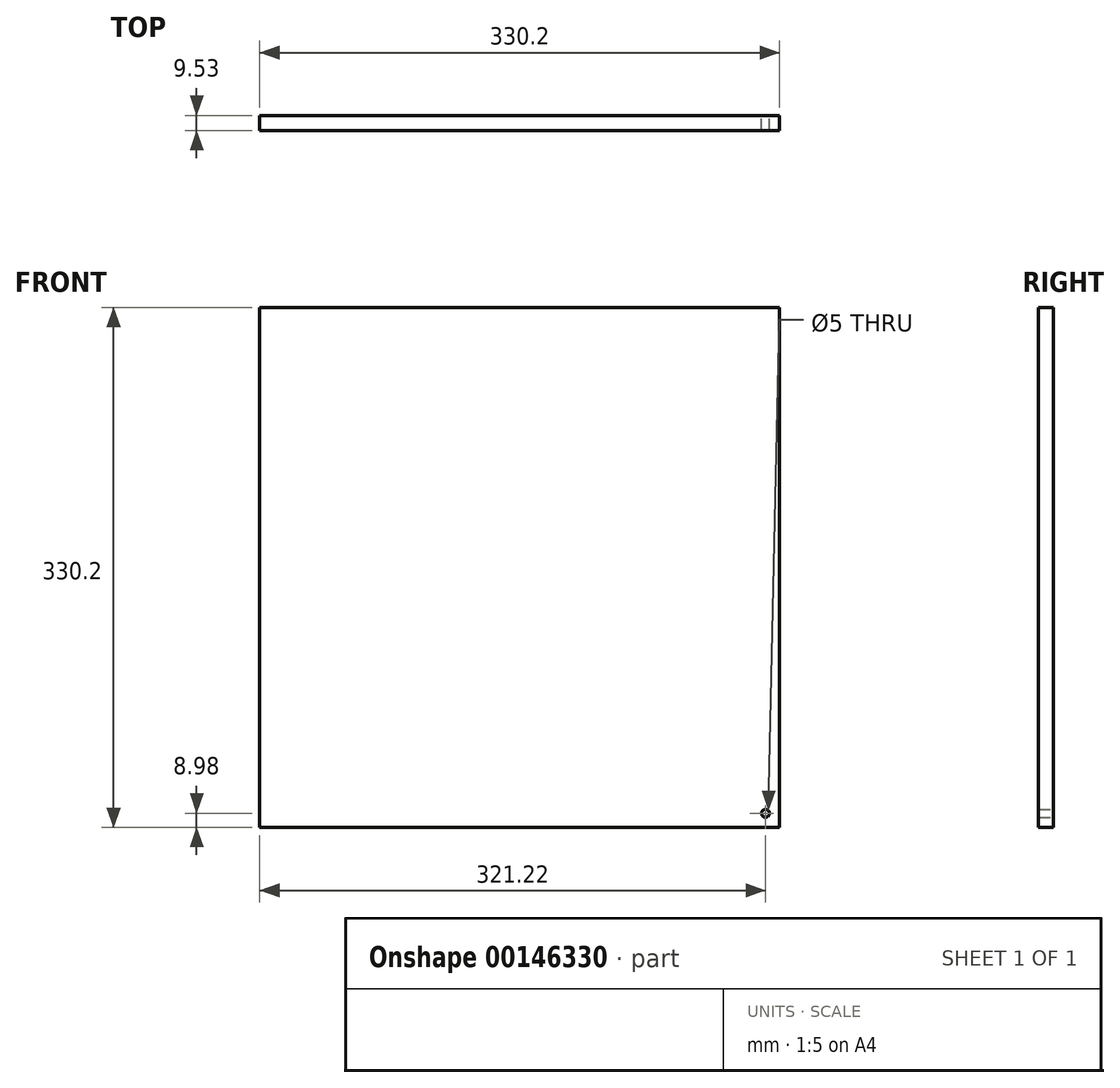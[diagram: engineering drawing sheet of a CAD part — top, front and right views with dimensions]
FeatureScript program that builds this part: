
annotation { "Feature Type Name" : "Feature", "Feature Type Description" : "" }
export const myFeature = defineFeature(function(context is Context, id is Id, definition is map)
    precondition{}
    {
        {
            var Q0;
            Q0=qCreatedBy(makeId("Front.planeOp"),FACE);
            var sketch = newSketch(context, id + "F0", { "sketchPlane" : qUnion([Q0])});
            skLineSegment(sketch, "E0.bottom", {"start": v(0, 0) * mm, "end": v(330.2, 0) * mm});
            skLineSegment(sketch, "E0.top", {"start": v(0, 330.2) * mm, "end": v(330.2, 330.2) * mm});
            skLineSegment(sketch, "E0.left", {"start": v(0, 0) * mm, "end": v(0, 330.2) * mm});
            skLineSegment(sketch, "E0.right", {"start": v(330.2, 0) * mm, "end": v(330.2, 330.2) * mm});
            skSolve(sketch);
        }
        {
            var Q0;
            Q0 = qSketchRegion(id + "F0", true);
            var Q1;
            Q1=makeQuery(id+"F0.imprint","IMPRINT",FACE,{"disambiguationData":[TD([[makeQuery(id+"F0.imprint","IMPRINT",EDGE,{"derivedFrom":sQuery(id+"F0.wireOp",EDGE,"E0.bottom")}),1.0]])]});
            extrude(context, id + "F1", {"entities" : qUnion([Q0, Q1]), "depth" : 9.52 * mm});
        }
        {
            var Q0;
            Q0=makeQuery(id+"F1.opExtrude","CAP_FACE",FACE,{"disambiguationData":[OSD([sQuery(id+"F0.wireOp",EDGE,"E0.bottom"),sQuery(id+"F0.wireOp",EDGE,"E0.top"),sQuery(id+"F0.wireOp",EDGE,"E0.left"),sQuery(id+"F0.wireOp",EDGE,"E0.right")])],"isStart":true});
            var sketch = newSketch(context, id + "F2", { "sketchPlane" : qUnion([Q0])});
            skLineSegment(sketch, "E1", {"start": v(-330.2, 0) * mm, "end": v(-321.22, 8.98) * mm});
            skLineSegment(sketch, "E2", {"start": v(0, 0) * mm, "end": v(-330.2, 330.2) * mm});
            skLineSegment(sketch, "E3", {"start": v(-330.2, 0) * mm, "end": v(0, 330.2) * mm});
            skCircle(sketch, "E4", {"center": v(-165.1, 165.1) * mm, "radius": 220.79 * mm});
            skSolve(sketch);
        }
        {
            var Q0;
            Q0=sQuery(id+"F2.wireOp",VERTEX,"E1.end");
            var Q1;
            Q1=makeQuery(id+"F1.opExtrude","SWEPT_BODY",BODY,{"disambiguationData":[OSD([sQuery(id+"F0.wireOp",EDGE,"E0.bottom"),sQuery(id+"F0.wireOp",EDGE,"E0.top"),sQuery(id+"F0.wireOp",EDGE,"E0.left"),sQuery(id+"F0.wireOp",EDGE,"E0.right")])]});
            hole(context, id + "F3", {"style" : HoleStyle.SIMPLE, "endStyle" : HoleEndStyle.THROUGH, "holeDiameter" : 5 * mm, "locations" : qUnion([Q0]), "scope" : qUnion([Q1]), "isTappedThrough" : true});
        }
    });
